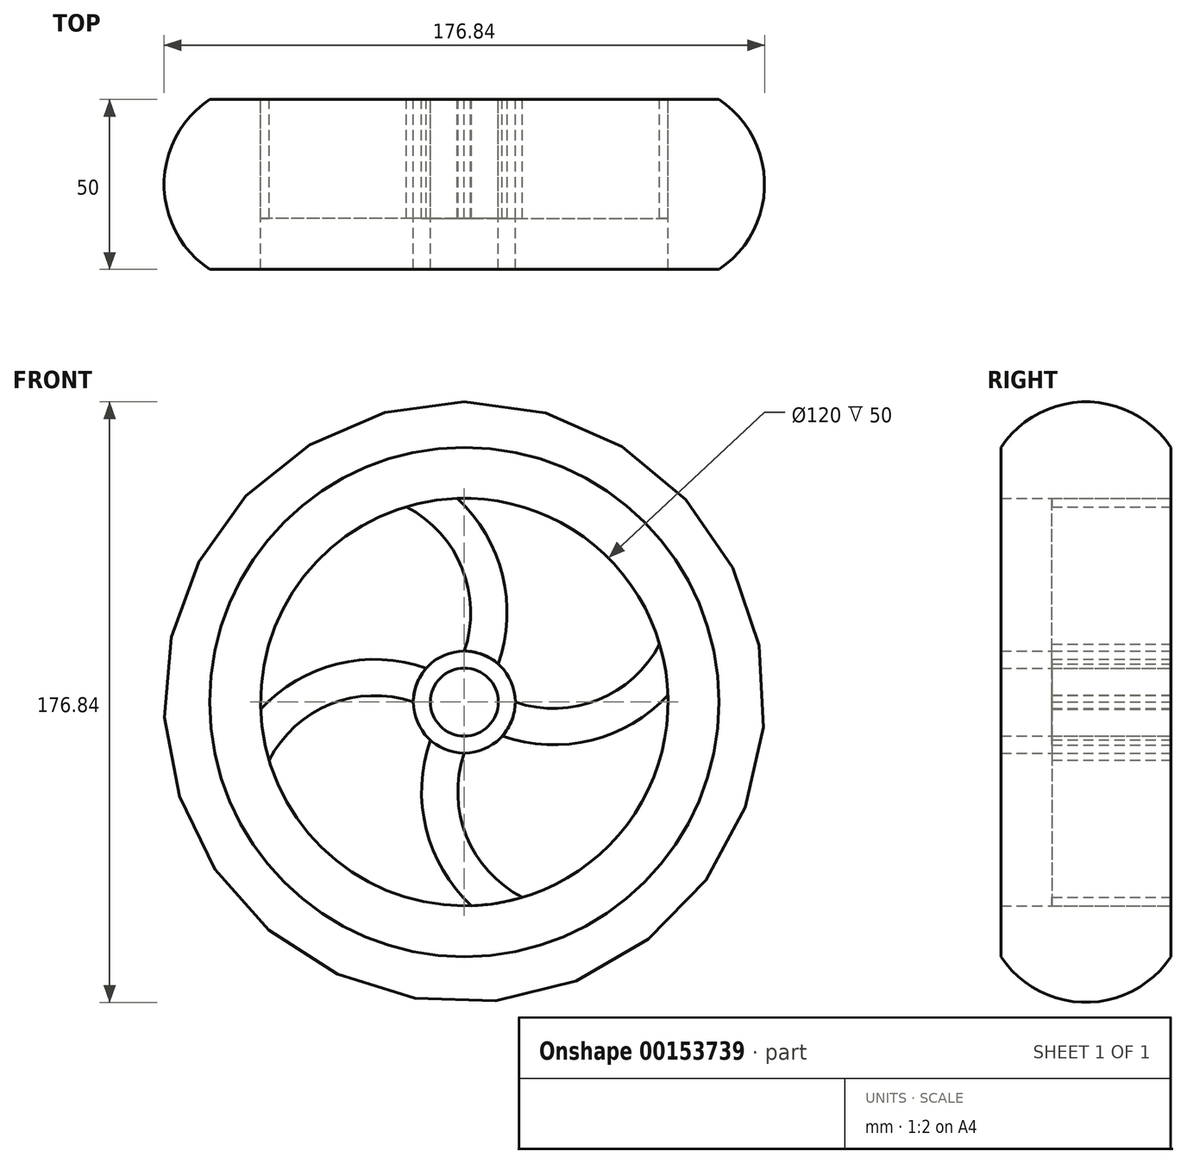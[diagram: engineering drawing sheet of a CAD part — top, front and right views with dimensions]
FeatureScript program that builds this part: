
annotation { "Feature Type Name" : "Feature", "Feature Type Description" : "" }
export const myFeature = defineFeature(function(context is Context, id is Id, definition is map)
    precondition{}
    {
        {
            var Q0;
            Q0=qCreatedBy(makeId("Front.planeOp"),FACE);
            var sketch = newSketch(context, id + "F0", { "sketchPlane" : qUnion([Q0])});
            skCircle(sketch, "E0", {"center": v(0, 0) * mm, "radius": 75 * mm});
            skArc(sketch, "E1", {"start": v(-17.13, 57.5) * mm, "mid": v(-48.73, 35) * mm, "end": v(-59.96, -2.13) * mm});
            skCircle(sketch, "E2", {"center": v(0, 0) * mm, "radius": 10 * mm});
            skArc(sketch, "E3", {"start": v(0, 15) * mm, "mid": v(-6.12, 13.7) * mm, "end": v(-11.18, 10) * mm});
            skArc(sketch, "E4", {"start": v(0, 15) * mm, "mid": v(-0.64, 39.44) * mm, "end": v(-17.13, 57.5) * mm});
            skArc(sketch, "E5", {"start": v(10, 11.18) * mm, "mid": v(11.24, 37.39) * mm, "end": v(-2.13, 59.96) * mm});
            skArc(sketch, "E6", {"start": v(-15, 0) * mm, "mid": v(-39.44, -0.64) * mm, "end": v(-57.5, -17.13) * mm});
            skArc(sketch, "E7", {"start": v(-11.18, 10) * mm, "mid": v(-37.39, 11.24) * mm, "end": v(-59.96, -2.13) * mm});
            skArc(sketch, "E8", {"start": v(0, -15) * mm, "mid": v(0.64, -39.44) * mm, "end": v(17.13, -57.5) * mm});
            skArc(sketch, "E9", {"start": v(-10, -11.18) * mm, "mid": v(-11.24, -37.39) * mm, "end": v(2.13, -59.96) * mm});
            skArc(sketch, "E10", {"start": v(15, 0) * mm, "mid": v(39.44, 0.64) * mm, "end": v(57.5, 17.13) * mm});
            skArc(sketch, "E11", {"start": v(11.18, -10) * mm, "mid": v(37.39, -11.24) * mm, "end": v(59.96, 2.13) * mm});
            skArc(sketch, "E12.trimOffspring", {"start": v(15, 0) * mm, "mid": v(13.7, 6.12) * mm, "end": v(10, 11.18) * mm});
            skArc(sketch, "E13.trimOffspring", {"start": v(57.5, 17.13) * mm, "mid": v(35, 48.73) * mm, "end": v(-2.13, 59.96) * mm});
            skArc(sketch, "E14.trimOffspring", {"start": v(0, -15) * mm, "mid": v(6.12, -13.7) * mm, "end": v(11.18, -10) * mm});
            skArc(sketch, "E15.trimOffspring", {"start": v(17.13, -57.5) * mm, "mid": v(48.73, -35) * mm, "end": v(59.96, 2.13) * mm});
            skArc(sketch, "E16.trimOffspring", {"start": v(-15, 0) * mm, "mid": v(-13.7, -6.12) * mm, "end": v(-10, -11.18) * mm});
            skArc(sketch, "E17.trimOffspring", {"start": v(-57.5, -17.13) * mm, "mid": v(-35, -48.73) * mm, "end": v(2.13, -59.96) * mm});
            skSolve(sketch);
        }
        {
            var Q0;
            Q0 = qSketchRegion(id + "F0", true);
            extrude(context, id + "F1", {"entities" : qUnion([Q0]), "depth" : 50 * mm});
        }
        {
            var Q0;
            Q0=qCreatedBy(makeId("Right.planeOp"),FACE);
            var sketch = newSketch(context, id + "F2", { "sketchPlane" : qUnion([Q0])});
            skArc(sketch, "E18", {"start": v(0, 75) * mm, "mid": v(-25, 88.42) * mm, "end": v(-50, 75) * mm});
            skLineSegment(sketch, "E19", {"start": v(0, 75) * mm, "end": v(0, 0) * mm, "construction": true});
            skLineSegment(sketch, "E20", {"start": v(0, 0) * mm, "end": v(-50, 0) * mm, "construction": true});
            skLineSegment(sketch, "E21", {"start": v(-50, 0) * mm, "end": v(-50, 75) * mm, "construction": true});
            skLineSegment(sketch, "E22", {"start": v(-50, 75) * mm, "end": v(0, 75) * mm});
            skSolve(sketch);
        }
        {
            var Q0;
            Q0 = qSketchRegion(id + "F2", true);
            var Q1;
            Q1=sQuery(id+"F2.wireOp",EDGE,"E20");
            revolve(context, id + "F3", {"operationType" : NewBodyOperationType.ADD, "entities" : qUnion([Q0]), "axis" : qUnion([Q1]), "revolveType" : RevolveType.FULL});
        }
        {
            var Q0;
            Q0=qCreatedBy(makeId("Front.planeOp"),FACE);
            cPlane(context, id + "F4", {"entities" : qUnion([Q0]), "cplaneType" : CPlaneType.OFFSET, "offset" : 25 * mm, "width" : 150 * mm, "height" : 150 * mm});
        }
        {
            var Q0;
            Q0=makeQuery(id+"F1.opExtrude","CAP_FACE",FACE,{"disambiguationData":[OSD([sQuery(id+"F0.wireOp",EDGE,"E0"),sQuery(id+"F0.wireOp",EDGE,"E1"),sQuery(id+"F0.wireOp",EDGE,"E2"),sQuery(id+"F0.wireOp",EDGE,"E3"),sQuery(id+"F0.wireOp",EDGE,"E4"),sQuery(id+"F0.wireOp",EDGE,"E5"),sQuery(id+"F0.wireOp",EDGE,"E6"),sQuery(id+"F0.wireOp",EDGE,"E7"),sQuery(id+"F0.wireOp",EDGE,"E8"),sQuery(id+"F0.wireOp",EDGE,"E9"),sQuery(id+"F0.wireOp",EDGE,"E10"),sQuery(id+"F0.wireOp",EDGE,"E11"),sQuery(id+"F0.wireOp",EDGE,"E12.trimOffspring"),sQuery(id+"F0.wireOp",EDGE,"E13.trimOffspring"),sQuery(id+"F0.wireOp",EDGE,"E14.trimOffspring"),sQuery(id+"F0.wireOp",EDGE,"E15.trimOffspring"),sQuery(id+"F0.wireOp",EDGE,"E16.trimOffspring"),sQuery(id+"F0.wireOp",EDGE,"E17.trimOffspring")])],"isStart":false});
            var sketch = newSketch(context, id + "F5", { "sketchPlane" : qUnion([Q0])});
            skArc(sketch, "E23.0", {"start": v(0, 15) * mm, "mid": v(-0.64, 39.44) * mm, "end": v(-17.13, 57.5) * mm});
            skArc(sketch, "E23.1", {"start": v(10, 11.18) * mm, "mid": v(11.24, 37.39) * mm, "end": v(-2.13, 59.96) * mm});
            skArc(sketch, "E23.2", {"start": v(15, 0) * mm, "mid": v(39.44, 0.64) * mm, "end": v(57.5, 17.13) * mm});
            skArc(sketch, "E23.3", {"start": v(11.18, -10) * mm, "mid": v(37.39, -11.24) * mm, "end": v(59.96, 2.13) * mm});
            skArc(sketch, "E23.4", {"start": v(0, -15) * mm, "mid": v(0.64, -39.44) * mm, "end": v(17.13, -57.5) * mm});
            skArc(sketch, "E23.5", {"start": v(-10, -11.18) * mm, "mid": v(-11.24, -37.39) * mm, "end": v(2.13, -59.96) * mm});
            skArc(sketch, "E23.6", {"start": v(-15, 0) * mm, "mid": v(-39.44, -0.64) * mm, "end": v(-57.5, -17.13) * mm});
            skArc(sketch, "E23.7", {"start": v(-11.18, 10) * mm, "mid": v(-37.39, 11.24) * mm, "end": v(-59.96, -2.13) * mm});
            skArc(sketch, "E24", {"start": v(-11.18, 10) * mm, "mid": v(-14.01, 5.35) * mm, "end": v(-15, 0) * mm});
            skArc(sketch, "E25", {"start": v(-59.96, -2.13) * mm, "mid": v(-59.2, -9.7) * mm, "end": v(-57.5, -17.13) * mm});
            skArc(sketch, "E26.trimOffspring", {"start": v(-2.13, 59.96) * mm, "mid": v(-9.7, 59.2) * mm, "end": v(-17.13, 57.5) * mm});
            skArc(sketch, "E27.trimOffspring", {"start": v(59.96, 2.13) * mm, "mid": v(59.2, 9.7) * mm, "end": v(57.5, 17.13) * mm});
            skArc(sketch, "E28.trimOffspring", {"start": v(2.13, -59.96) * mm, "mid": v(9.7, -59.2) * mm, "end": v(17.13, -57.5) * mm});
            skArc(sketch, "E29.trimOffspring", {"start": v(10, 11.18) * mm, "mid": v(5.35, 14.01) * mm, "end": v(0, 15) * mm});
            skArc(sketch, "E30.trimOffspring", {"start": v(11.18, -10) * mm, "mid": v(14.01, -5.35) * mm, "end": v(15, 0) * mm});
            skArc(sketch, "E31.trimOffspring", {"start": v(-10, -11.18) * mm, "mid": v(-5.35, -14.01) * mm, "end": v(0, -15) * mm});
            skSolve(sketch);
        }
        {
            var Q0;
            Q0 = qSketchRegion(id + "F5", true);
            extrude(context, id + "F6", {"entities" : qUnion([Q0]), "operationType" : NewBodyOperationType.REMOVE, "oppositeDirection" : true, "depth" : 15 * mm});
        }
    });
